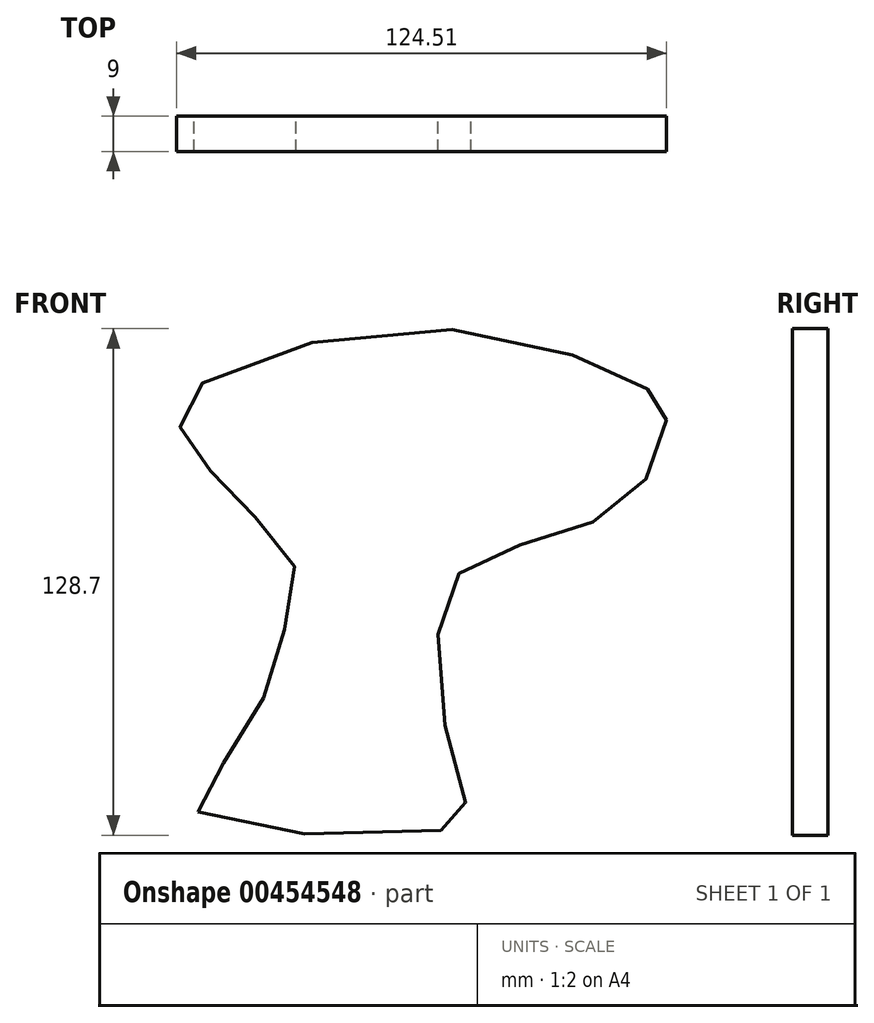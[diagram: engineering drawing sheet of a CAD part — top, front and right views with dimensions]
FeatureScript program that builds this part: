
annotation { "Feature Type Name" : "Feature", "Feature Type Description" : "" }
export const myFeature = defineFeature(function(context is Context, id is Id, definition is map)
    precondition{}
    {
        {
            var Q0;
            Q0=qCreatedBy(makeId("Front.planeOp"),FACE);
            var sketch = newSketch(context, id + "F0", { "sketchPlane" : qUnion([Q0])});
            skFitSpline(sketch, "E0", {"points": [v(-179.48, 3) * mm, v(-169.68, 19.24) * mm, v(-158.96, 44.96) * mm, v(-155.29, 66.4) * mm, v(-170.3, 82.63) * mm, v(-181.32, 96.71) * mm, v(-184.38, 106.51) * mm, v(-120.07, 125.8) * mm, v(-65.26, 110.5) * mm, v(-60.66, 105.6) * mm, v(-64.95, 88.75) * mm, v(-85.16, 74.36) * mm, v(-111.5, 65.17) * mm, v(-118.54, 44.65) * mm, v(-111.8, 6.07) * mm, v(-111.5, 0) * mm, v(-179.48, 3) * mm]});
            skSolve(sketch);
        }
        {
            var Q0;
            Q0 = qSketchRegion(id + "F0", true);
            extrude(context, id + "F1", {"entities" : qUnion([Q0]), "depth" : 9 * mm});
        }
    });
